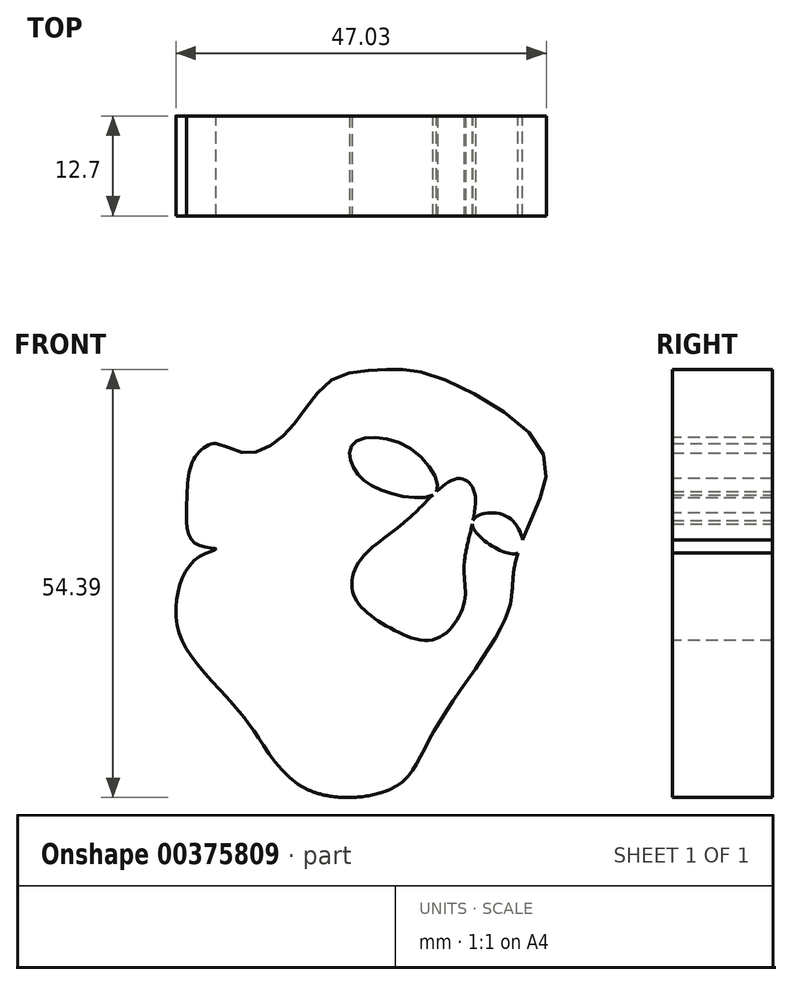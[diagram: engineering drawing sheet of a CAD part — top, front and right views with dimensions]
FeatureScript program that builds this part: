
annotation { "Feature Type Name" : "Feature", "Feature Type Description" : "" }
export const myFeature = defineFeature(function(context is Context, id is Id, definition is map)
    precondition{}
    {
        {
            var Q0;
            Q0=qCreatedBy(makeId("Front.planeOp"),FACE);
            var sketch = newSketch(context, id + "F0", { "sketchPlane" : qUnion([Q0])});
            skFitSpline(sketch, "E0", {"points": [v(3.2, 27.63) * mm, v(0, 28.75) * mm, v(-2.82, 26.74) * mm, v(-3.72, 20.7) * mm, v(-2.6, 16.02) * mm, v(0, 15.35) * mm, v(-2.6, 14) * mm, v(-5.06, 7.98) * mm, v(-3.72, 2.62) * mm, v(2.09, -4.3) * mm, v(5.66, -9) * mm, v(11.7, -15.24) * mm, v(22.86, -14.8) * mm, v(27.77, -7.65) * mm, v(36.92, 6.86) * mm, v(37.82, 12.45) * mm, v(40.05, 19.14) * mm, v(41.39, 27.85) * mm, v(27.32, 37.45) * mm, v(21.3, 38.12) * mm, v(15.04, 37) * mm, v(10.57, 32.1) * mm, v(7, 28.52) * mm, v(3.2, 27.63) * mm]});
            skFitSpline(sketch, "E1", {"points": [v(24.42, 19.14) * mm, v(18.39, 14) * mm, v(17.5, 9.54) * mm, v(21.74, 5.52) * mm, v(28, 3.96) * mm, v(31.56, 8.65) * mm, v(31.56, 13.78) * mm, v(32.9, 22.27) * mm, v(30.67, 24.28) * mm, v(24.42, 19.14) * mm]});
            skFitSpline(sketch, "E2", {"points": [v(24.42, 19.14) * mm, v(24.42, 16.02) * mm, v(26.43, 13.34) * mm, v(31.56, 13.78) * mm], "startDerivative": vector(-1.28, -10.27) * mm, "endDerivative": vector(14.8, 3.88) * mm});
            skFitSpline(sketch, "E3", {"points": [v(17.5, 9.54) * mm, v(24.42, 9.54) * mm, v(28, 3.96) * mm], "startDerivative": vector(15.33, 2.85) * mm, "endDerivative": vector(5.62, -14.08) * mm});
            skFitSpline(sketch, "E4", {"points": [v(17.5, 25.62) * mm, v(21.96, 22.5) * mm, v(28, 22.62) * mm, v(24.42, 28.3) * mm, v(17.5, 28.75) * mm, v(17.5, 25.62) * mm]});
            skFitSpline(sketch, "E5", {"points": [v(32.57, 18.54) * mm, v(38.36, 14.82) * mm, v(37.15, 19.37) * mm, v(32.57, 18.54) * mm]});
            skFitSpline(sketch, "E6", {"points": [v(-3.72, 20.7) * mm, v(-7.29, 14.9) * mm, v(-5.06, 7.98) * mm], "startDerivative": vector(-10.13, -11.35) * mm, "endDerivative": vector(7.36, -14.09) * mm});
            skFitSpline(sketch, "E7", {"points": [v(0, 28.75) * mm, v(7.23, 40.36) * mm, v(15.49, 47.28) * mm, v(27.77, 45.27) * mm, v(42.28, 35.9) * mm, v(48.76, 24.5) * mm, v(48.09, 22.72) * mm, v(44.74, 24.73) * mm, v(42.28, 14.45) * mm, v(37.63, 10.05) * mm], "startDerivative": vector(51, 89.39) * mm, "endDerivative": vector(-60.3, -27.81) * mm});
            skFitSpline(sketch, "E8", {"points": [v(22.86, -14.8) * mm, v(24.64, -20.82) * mm, v(37.82, -27.75) * mm, v(48.53, -33.55) * mm, v(52.55, -44.72) * mm, v(55, -49.4) * mm, v(56.57, -55.3) * mm], "startDerivative": vector(2.55, -45.1) * mm, "endDerivative": vector(8.93, -46.65) * mm});
            skFitSpline(sketch, "E9", {"points": [v(-5.06, 6.7) * mm, v(-8.18, 0) * mm, v(-14.66, -4.3) * mm, v(-28.28, -6.76) * mm], "startDerivative": vector(-8.47, -24.52) * mm, "endDerivative": vector(-36.7, -4.28) * mm});
            skFitSpline(sketch, "E10", {"points": [v(-34.08, -12.56) * mm, v(-28.28, -6.76) * mm, v(-25.15, 3.07) * mm, v(-19.35, 6.2) * mm, v(-19.57, 12.45) * mm, v(-18.68, 15.35) * mm, v(-21.58, 23.83) * mm, v(-28.28, 24.06) * mm, v(-24.93, 35.67) * mm, v(-26.5, 42.37) * mm, v(-28.28, 41.25) * mm, v(-34.75, 28.75) * mm, v(-40.11, 20.7) * mm], "startDerivative": vector(80.44, 52.2) * mm, "endDerivative": vector(-55.16, -72.67) * mm});
            skFitSpline(sketch, "E11", {"points": [v(-40.11, 20.7) * mm, v(-40.11, 18.47) * mm, v(-42.34, 7.98) * mm, v(-45.7, -4.3) * mm, v(-47.26, -4.3) * mm, v(-48.82, -6.76) * mm, v(-52.4, -6.76) * mm, v(-58.64, -14.8) * mm, v(-61.1, -21.72) * mm, v(-73.16, -37.35) * mm], "startDerivative": vector(2.67, -30.08) * mm, "endDerivative": vector(-79.64, -92.07) * mm});
            skFitSpline(sketch, "E12", {"points": [v(-61.1, -21.72) * mm, v(-48.82, -6.76) * mm], "startDerivative": vector(12.28, 14.96) * mm, "endDerivative": vector(12.28, 14.96) * mm});
            skFitSpline(sketch, "E13", {"points": [v(-53.96, -45.6) * mm, v(-33.64, -27.52) * mm, v(-32.3, -21.72) * mm, v(-34.08, -12.56) * mm], "startDerivative": vector(53.43, 41.78) * mm, "endDerivative": vector(-8.12, 34.55) * mm});
            skFitSpline(sketch, "E14", {"points": [v(0, -23.95) * mm, v(11.7, -15.24) * mm], "startDerivative": vector(11.7, 8.7) * mm, "endDerivative": vector(11.7, 8.7) * mm});
            skFitSpline(sketch, "E15", {"points": [v(14.82, -16.1) * mm, v(20.85, -30.65) * mm], "startDerivative": vector(6.02, -14.55) * mm, "endDerivative": vector(6.02, -14.55) * mm});
            skFitSpline(sketch, "E16", {"points": [v(20.85, -30.65) * mm, v(20.85, -15.24) * mm], "startDerivative": vector(0, 15.4) * mm, "endDerivative": vector(0, 15.4) * mm});
            skFitSpline(sketch, "E17", {"points": [v(0, -23.95) * mm, v(-9.74, -1.63) * mm], "startDerivative": vector(-9.74, 22.33) * mm, "endDerivative": vector(-9.74, 22.33) * mm});
            skFitSpline(sketch, "E18", {"points": [v(17.26, -21.98) * mm, v(16.56, -23.33) * mm, v(17.33, -29.3) * mm, v(17.6, -34.2) * mm, v(18.84, -37.15) * mm, v(20.73, -43.23) * mm, v(23.55, -55.3) * mm, v(22.58, -55.3) * mm], "startDerivative": vector(-10.95, -12.48) * mm, "endDerivative": vector(-17.78, 6.7) * mm});
            skPoint(sketch, "E19.1.internal.orphan", {"position": v(11.7, -23.95) * mm});
            skPoint(sketch, "E19.2.internal.orphan", {"position": v(9.68, -30.65) * mm});
            skPoint(sketch, "E19.3.internal.orphan", {"position": v(11.7, -46.95) * mm});
            skFitSpline(sketch, "E20", {"points": [v(6.72, -18.95) * mm, v(10.95, -23.95) * mm, v(10.53, -25.37) * mm, v(9.97, -29.64) * mm, v(9.68, -30.65) * mm], "startDerivative": vector(16.21, -15.96) * mm, "endDerivative": vector(-2.15, -5) * mm});
            skFitSpline(sketch, "E21", {"points": [v(9.68, -30.65) * mm, v(9.68, -45.14) * mm, v(9.97, -46.95) * mm, v(9.97, -55.3) * mm], "startDerivative": vector(-0.76, -38.9) * mm, "endDerivative": vector(-0.69, -28.55) * mm});
            skSolve(sketch);
        }
        {
            var Q0;
            {var subQ1=sQuery(id+"F0.wireOp",EDGE,"E0");var subQ7=makeQuery(id+"F0.imprint","IMPRINT",VERTEX,{"derivedFrom":subQ1});Q0=makeQuery(id+"F0.imprint","IMPRINT",FACE,{"disambiguationData":[TD([[makeQuery(id+"F0.imprint","IMPRINT",EDGE,{"disambiguationData":[TD([[subQ7,1.0]])],"derivedFrom":subQ1}),1.0]])]});}
            extrude(context, id + "F1", {"entities" : qUnion([Q0]), "depth" : 12.7 * mm});
        }
    });
